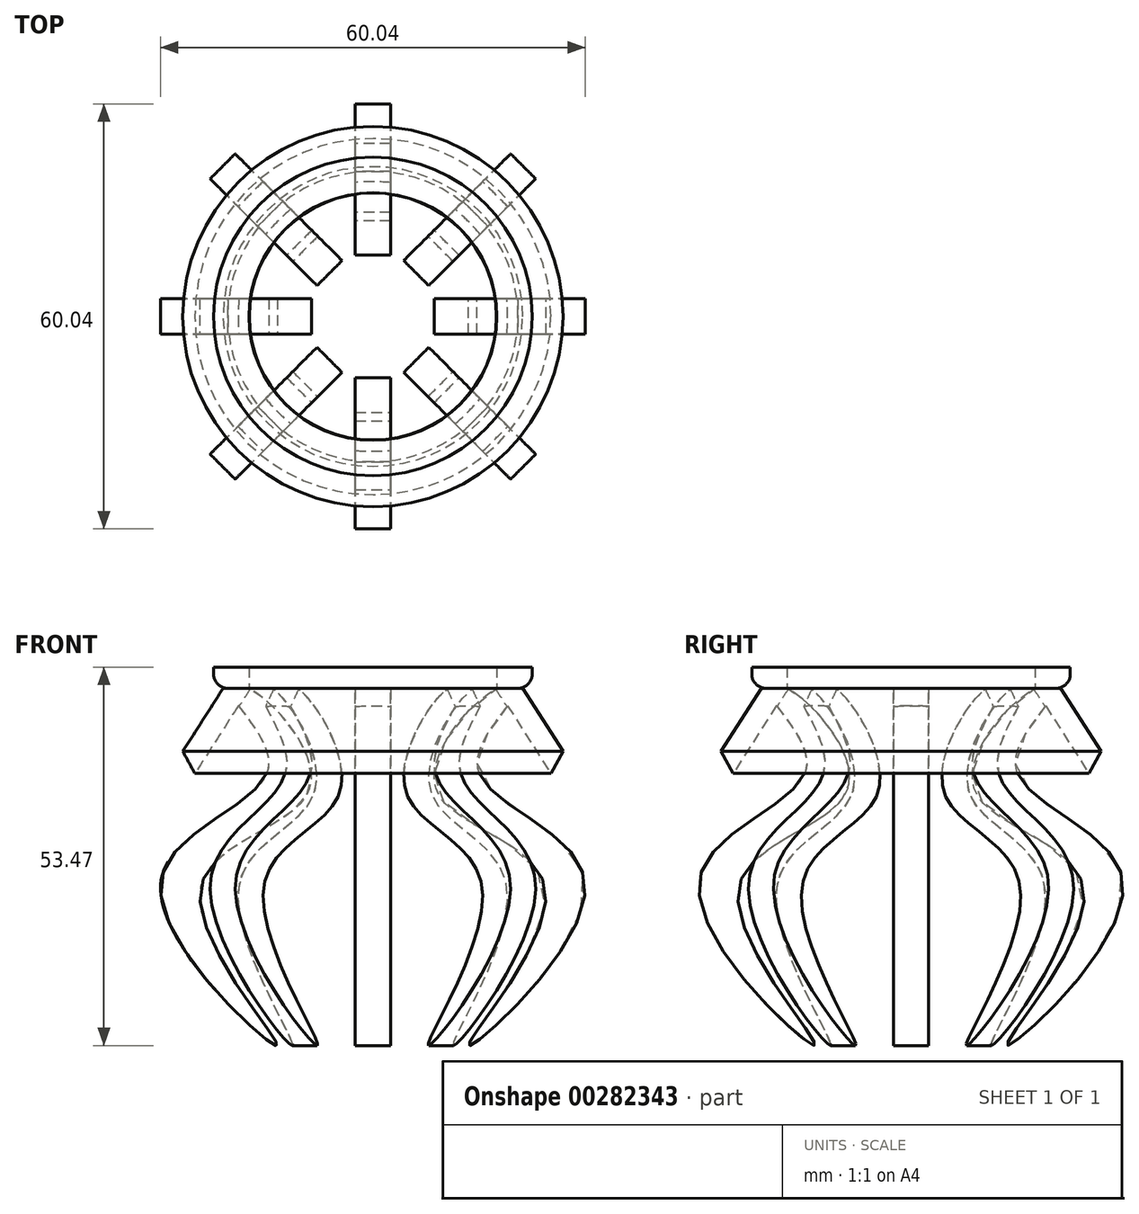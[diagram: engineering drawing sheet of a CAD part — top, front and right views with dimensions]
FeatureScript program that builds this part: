
annotation { "Feature Type Name" : "Feature", "Feature Type Description" : "" }
export const myFeature = defineFeature(function(context is Context, id is Id, definition is map)
    precondition{}
    {
        {
            var Q0;
            Q0=qCreatedBy(makeId("Top.planeOp"),FACE);
            var sketch = newSketch(context, id + "F0", { "sketchPlane" : qUnion([Q0])});
            skCircle(sketch, "E0", {"center": v(0, 0) * mm, "radius": 17.5 * mm});
            skCircle(sketch, "E1", {"center": v(0, 0) * mm, "radius": 22.5 * mm});
            skSolve(sketch);
        }
        {
            var Q0;
            Q0 = qSketchRegion(id + "F0", true);
            extrude(context, id + "F1", {"entities" : qUnion([Q0]), "depth" : 3 * mm});
        }
        {
            var Q0;
            Q0=makeQuery(id+"F1.opExtrude","CAP_EDGE",EDGE,{"disambiguationData":[OSD([sQuery(id+"F0.wireOp",EDGE,"E1")])],"isStart":true});
            fillet(context, id + "F2", {"entities" : qUnion([Q0]), "radius" : 2 * mm, "tangentPropagation" : true, "allowEdgeOverflow" : false});
        }
        {
            var Q0;
            Q0=qCreatedBy(makeId("Front.planeOp"),FACE);
            var sketch = newSketch(context, id + "F3", { "sketchPlane" : qUnion([Q0])});
            skLineSegment(sketch, "E2.1.0", {"start": v(-22.5, 3) * mm, "end": v(22.5, 3) * mm, "construction": true});
            skLineSegment(sketch, "E2.4.0", {"start": v(20.5, 0) * mm, "end": v(-20.5, 0) * mm, "construction": true});
            skFitSpline(sketch, "E3", {"points": [v(-20.5, 0) * mm, v(-14.8, -11.3) * mm, v(-30, -27.83) * mm, v(-13.55, -50.46) * mm, v(-24.4, -28.6) * mm, v(-9.02, -14.46) * mm, v(-17.54, 0) * mm, v(-20.5, 0) * mm]});
            skSolve(sketch);
        }
        {
            var Q0;
            Q0 = qSketchRegion(id + "F3", true);
            extrude(context, id + "F4", {"entities" : qUnion([Q0]), "operationType" : NewBodyOperationType.ADD, "depth" : 2.5 * mm, "hasSecondDirection" : true, "secondDirectionOppositeDirection" : true, "secondDirectionDepth" : 2.5 * mm});
        }
        {
            var Q0;
            Q0=makeQuery(id+"F1.opExtrude","SWEPT_BODY",BODY,{"disambiguationData":[OSD([sQuery(id+"F0.wireOp",EDGE,"E0"),sQuery(id+"F0.wireOp",EDGE,"E1")])]});
            var Q1;
            Q1=makeQuery(id+"F1.opExtrude","SWEPT_FACE",FACE,{"disambiguationData":[OSD([sQuery(id+"F0.wireOp",EDGE,"E0")])]});
            circularPattern(context, id + "F5", {"entities" : qUnion([Q0]), "axis" : qUnion([Q1]), "angle" : 360 * degree, "instanceCount" : 8, "equalSpace" : true});
        }
        {
            var Q0;
            Q0=qCreatedBy(makeId("Front.planeOp"),FACE);
            var sketch = newSketch(context, id + "F6", { "sketchPlane" : qUnion([Q0])});
            skLineSegment(sketch, "E4", {"start": v(-21.16, 0) * mm, "end": v(-29.32, -12.76) * mm});
            skLineSegment(sketch, "E5", {"start": v(-29.32, -12.76) * mm, "end": v(-25.61, -12.76) * mm});
            skLineSegment(sketch, "E6", {"start": v(-25.61, -12.76) * mm, "end": v(-17.45, 0) * mm});
            skLineSegment(sketch, "E7", {"start": v(-17.45, 0) * mm, "end": v(-21.16, 0) * mm});
            skSolve(sketch);
        }
        {
            var Q0;
            Q0 = qSketchRegion(id + "F6", true);
            var Q1;
            Q1=makeQuery(id+"F1.opExtrude","SWEPT_FACE",FACE,{"disambiguationData":[OSD([sQuery(id+"F0.wireOp",EDGE,"E0")])]});
            revolve(context, id + "F7", {"operationType" : NewBodyOperationType.ADD, "entities" : qUnion([Q0]), "axis" : qUnion([Q1]), "revolveType" : RevolveType.FULL});
        }
        {
            var Q0;
            Q0=makeQuery(id+"F7.opRevolve","SWEPT_EDGE",EDGE,{"disambiguationData":[OSD([sQuery(id+"F6.wireOp",EDGE,"E4"),sQuery(id+"F6.wireOp",EDGE,"E5")])]});
            chamfer(context, id + "F8", {"entities" : qUnion([Q0]), "width" : 2.5 * mm, "tangentPropagation" : true});
        }
    });
